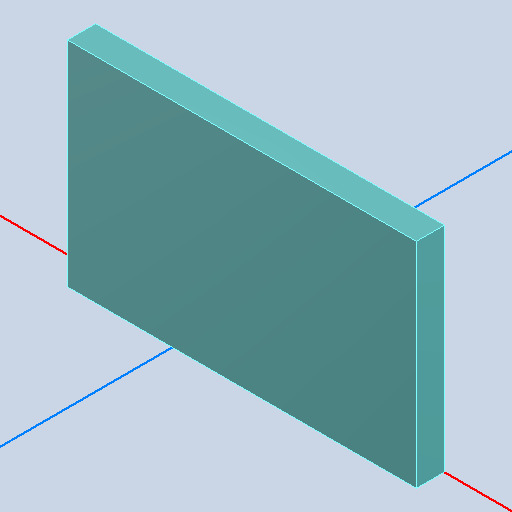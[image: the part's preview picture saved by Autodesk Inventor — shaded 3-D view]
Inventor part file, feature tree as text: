
AUTODESK INVENTOR PART (.ipt)
format: ipt  version: 2022 (Build 260153000, 153)  size: 92,672 bytes
history: native  units: mm
features: other x2, extrude x1
ambient origin geometry x8: Origin, YZ Plane, XZ Plane, XY Plane, X Axis, Y Axis, Z Axis, Center Point
bodies: Body1 (feature_tree)
feature tree (3):
  other  "Твердое тело1"
  extrude  "Выдавливание1"  Depth=1.0mm TaperAngle=0.0deg
  other  "SCREWTERMINAL-5MM-2, J1_SCREWTERMINAL-5MM-2_4"
